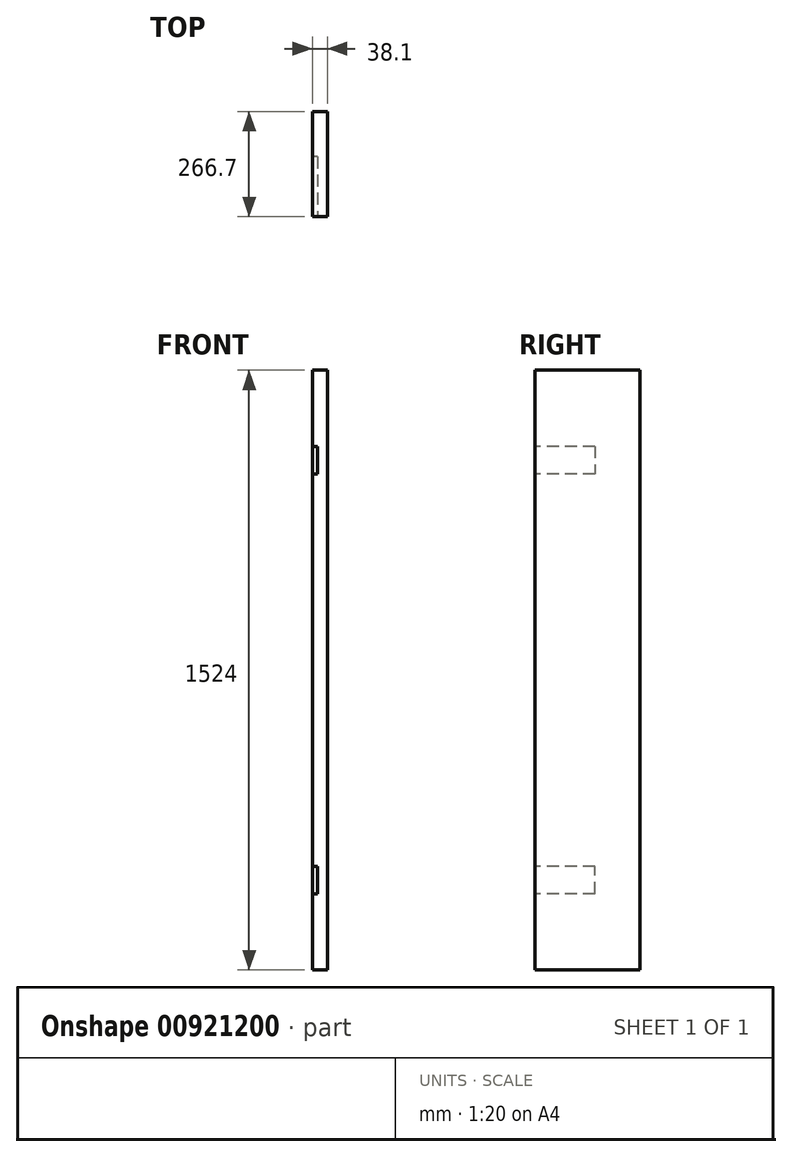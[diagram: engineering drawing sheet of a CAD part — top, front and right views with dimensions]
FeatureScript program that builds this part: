
annotation { "Feature Type Name" : "Feature", "Feature Type Description" : "" }
export const myFeature = defineFeature(function(context is Context, id is Id, definition is map)
    precondition{}
    {
        {
            var Q0;
            Q0=qCreatedBy(makeId("Top.planeOp"),FACE);
            var sketch = newSketch(context, id + "F0", { "sketchPlane" : qUnion([Q0])});
            skLineSegment(sketch, "E0.bottom", {"start": v(0, 0) * mm, "end": v(-38.1, 0) * mm});
            skLineSegment(sketch, "E0.top", {"start": v(0, 266.7) * mm, "end": v(-38.1, 266.7) * mm});
            skLineSegment(sketch, "E0.left", {"start": v(0, 0) * mm, "end": v(0, 266.7) * mm});
            skLineSegment(sketch, "E0.right", {"start": v(-38.1, 0) * mm, "end": v(-38.1, 266.7) * mm});
            skSolve(sketch);
        }
        {
            var Q0;
            Q0 = qSketchRegion(id + "F0", true);
            extrude(context, id + "F1", {"entities" : qUnion([Q0]), "depth" : 1524 * mm, "offsetDistance" : 25.4 * mm});
        }
        {
            var Q0;
            Q0=makeQuery(id+"F1.opExtrude","SWEPT_FACE",FACE,{"disambiguationData":[OSD([sQuery(id+"F0.wireOp",EDGE,"E0.right")])]});
            var sketch = newSketch(context, id + "F2", { "sketchPlane" : qUnion([Q0])});
            skLineSegment(sketch, "E1.bottom", {"start": v(-152.4, 193.68) * mm, "end": v(0, 193.68) * mm});
            skLineSegment(sketch, "E1.top", {"start": v(-152.4, 263.53) * mm, "end": v(0, 263.53) * mm});
            skLineSegment(sketch, "E1.left", {"start": v(-152.4, 193.68) * mm, "end": v(-152.4, 263.53) * mm});
            skLineSegment(sketch, "E1.right", {"start": v(0, 193.68) * mm, "end": v(0, 263.53) * mm});
            skLineSegment(sketch, "E2", {"start": v(0, 762) * mm, "end": v(-266.7, 762) * mm, "construction": true});
            skLineSegment(sketch, "E3", {"start": v(0, 228.6) * mm, "end": v(-152.4, 228.6) * mm, "construction": true});
            skLineSegment(sketch, "E4.MirrorCS", {"start": v(-152.4, 1330.33) * mm, "end": v(-152.4, 1260.47) * mm});
            skLineSegment(sketch, "E5.MirrorCS", {"start": v(0, 1330.33) * mm, "end": v(0, 1260.48) * mm});
            skLineSegment(sketch, "E6.MirrorCS", {"start": v(-152.4, 1330.33) * mm, "end": v(0, 1330.33) * mm});
            skLineSegment(sketch, "E7.MirrorCS", {"start": v(-152.4, 1260.48) * mm, "end": v(0, 1260.48) * mm});
            skLineSegment(sketch, "E8.MirrorCS", {"start": v(0, 1295.4) * mm, "end": v(-152.4, 1295.4) * mm, "construction": true});
            skSolve(sketch);
        }
        {
            var Q0;
            Q0 = qSketchRegion(id + "F2", true);
            extrude(context, id + "F3", {"entities" : qUnion([Q0]), "operationType" : NewBodyOperationType.REMOVE, "oppositeDirection" : true, "depth" : 12.7 * mm, "offsetDistance" : 25.4 * mm});
        }
    });
